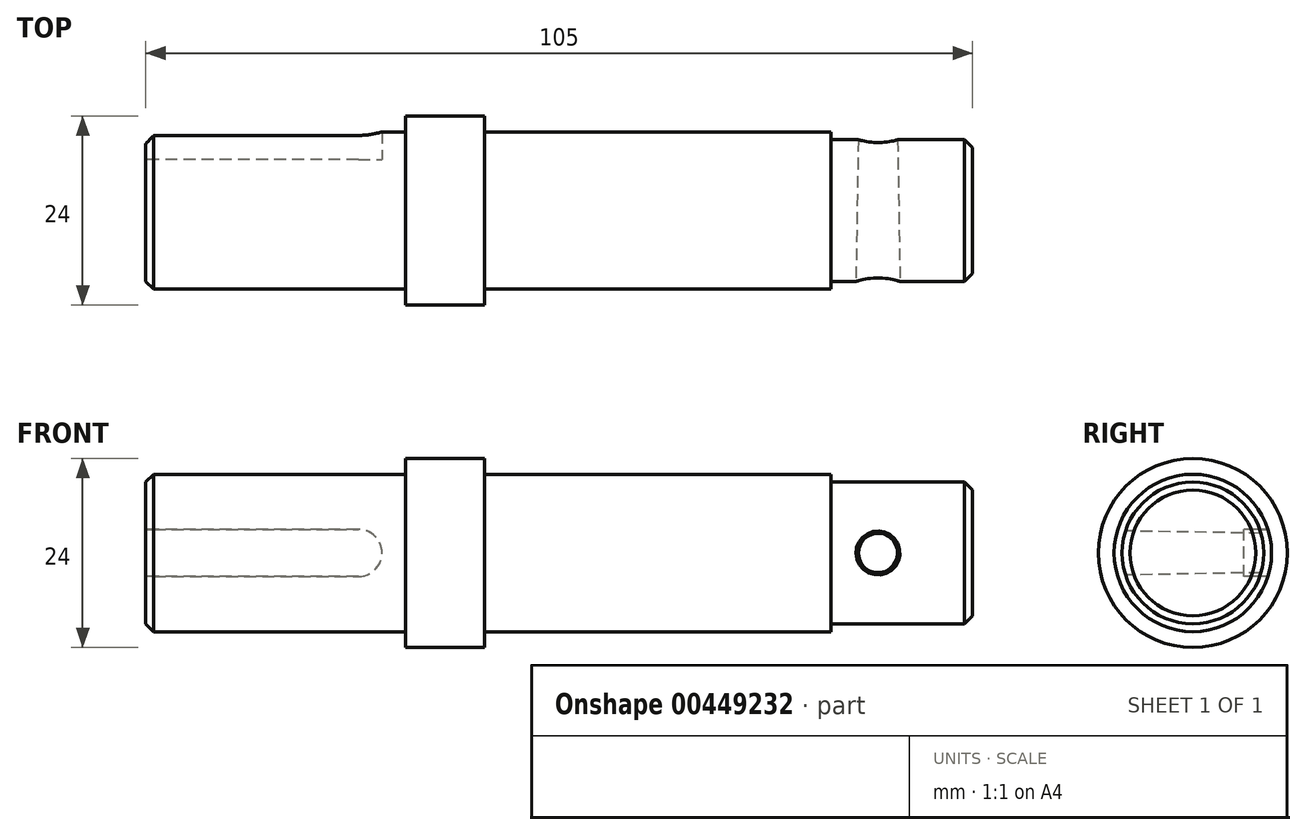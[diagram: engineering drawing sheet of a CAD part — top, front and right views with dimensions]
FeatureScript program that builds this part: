
annotation { "Feature Type Name" : "Feature", "Feature Type Description" : "" }
export const myFeature = defineFeature(function(context is Context, id is Id, definition is map)
    precondition{}
    {
        {
            var Q0;
            Q0=qCreatedBy(makeId("Right.planeOp"),FACE);
            var sketch = newSketch(context, id + "F0", { "sketchPlane" : qUnion([Q0])});
            skCircle(sketch, "E0", {"center": v(0, 0) * mm, "radius": 12 * mm});
            skSolve(sketch);
        }
        {
            var Q0;
            Q0 = qSketchRegion(id + "F0", true);
            extrude(context, id + "F1", {"entities" : qUnion([Q0]), "depth" : (105 - 18 - 33 - 44) * mm});
        }
        {
            var Q0;
            Q0=makeQuery(id+"F1.opExtrude","CAP_FACE",FACE,{"disambiguationData":[OSD([sQuery(id+"F0.wireOp",EDGE,"E0")])],"isStart":true});
            var sketch = newSketch(context, id + "F2", { "sketchPlane" : qUnion([Q0])});
            skCircle(sketch, "E1", {"center": v(0, 0) * mm, "radius": 10 * mm});
            skSolve(sketch);
        }
        {
            var Q0;
            Q0 = qSketchRegion(id + "F2", true);
            extrude(context, id + "F3", {"entities" : qUnion([Q0]), "operationType" : NewBodyOperationType.ADD, "depth" : 33 * mm});
        }
        {
            var Q0;
            Q0 = qSketchRegion(id + "F2", true);
            extrude(context, id + "F4", {"entities" : qUnion([Q0]), "operationType" : NewBodyOperationType.ADD, "oppositeDirection" : true, "depth" : (105 - 18 - 33) * mm});
        }
        {
            var Q0;
            Q0=makeQuery(id+"F4.opExtrude","CAP_FACE",FACE,{"disambiguationData":[OSD([sQuery(id+"F2.wireOp",EDGE,"E1")])],"isStart":false});
            var sketch = newSketch(context, id + "F5", { "sketchPlane" : qUnion([Q0])});
            skCircle(sketch, "E2", {"center": v(0, 0) * mm, "radius": 9 * mm});
            skSolve(sketch);
        }
        {
            var Q0;
            Q0 = qSketchRegion(id + "F5", true);
            extrude(context, id + "F6", {"entities" : qUnion([Q0]), "operationType" : NewBodyOperationType.ADD, "depth" : 18 * mm});
        }
        {
            var Q0;
            Q0=qCreatedBy(makeId("Front.planeOp"),FACE);
            cPlane(context, id + "F7", {"entities" : qUnion([Q0]), "cplaneType" : CPlaneType.OFFSET, "offset" : 6.5 * mm, "oppositeDirection" : true, "width" : 150 * mm, "height" : 150 * mm});
        }
        {
            var Q0;
            Q0=qCreatedBy(id+"F7.planeOp",FACE);
            var sketch = newSketch(context, id + "F8", { "sketchPlane" : qUnion([Q0])});
            skLineSegment(sketch, "E3.0", {"start": v(-33, -3) * mm, "end": v(-33, 3) * mm});
            skLineSegment(sketch, "E4.bottom", {"start": v(-6, -3) * mm, "end": v(-33, -3) * mm});
            skLineSegment(sketch, "E4.top", {"start": v(-6, 3) * mm, "end": v(-33, 3) * mm});
            skPoint(sketch, "E4.middle", {"position": v(-33, 0) * mm});
            skArc(sketch, "E5", {"start": v(-6, -3) * mm, "mid": v(-3, 0) * mm, "end": v(-6, 3) * mm});
            skPoint(sketch, "E5.centerSnap0", {"position": v(-3, 0) * mm});
            skPoint(sketch, "E6.orphan", {"position": v(-3, 3) * mm});
            skPoint(sketch, "E7.orphan", {"position": v(-3, -3) * mm});
            skPoint(sketch, "E4.right.end.orphan", {"position": v(-63, 3) * mm});
            skPoint(sketch, "E4.right.start.orphan", {"position": v(-63, -3) * mm});
            skPoint(sketch, "E8.orphan", {"position": v(-33, 10) * mm});
            skPoint(sketch, "E9.orphan", {"position": v(-33, -10) * mm});
            skSolve(sketch);
        }
        {
            var Q0;
            Q0 = qSketchRegion(id + "F8", true);
            extrude(context, id + "F9", {"entities" : qUnion([Q0]), "operationType" : NewBodyOperationType.REMOVE, "endBound" : BoundingType.THROUGH_ALL, "oppositeDirection" : true, "depth" : 25 * mm});
        }
        {
            var Q0;
            Q0=makeQuery(id+"F3.opExtrude","CAP_EDGE",EDGE,{"disambiguationData":[OSD([sQuery(id+"F2.wireOp",EDGE,"E1")])],"isStart":false});
            var Q1;
            Q1=makeQuery(id+"F6.opExtrude","CAP_EDGE",EDGE,{"disambiguationData":[OSD([sQuery(id+"F5.wireOp",EDGE,"E2")])],"isStart":false});
            chamfer(context, id + "F10", {"entities" : qUnion([Q0, Q1]), "width" : 1 * mm, "tangentPropagation" : true});
        }
        {
            var Q0;
            Q0=qCreatedBy(makeId("Top.planeOp"),FACE);
            var sketch = newSketch(context, id + "F11", { "sketchPlane" : qUnion([Q0])});
            skLineSegment(sketch, "E10", {"start": v(60, 13.35) * mm, "end": v(60, -14.26) * mm, "construction": true});
            skLineSegment(sketch, "E11", {"start": v(60, 9) * mm, "end": v(71, 9) * mm});
            skLineSegment(sketch, "E12", {"start": v(62.5, 9) * mm, "end": v(62.8, -9) * mm});
            skLineSegment(sketch, "E13", {"start": v(62.8, -9) * mm, "end": v(60, -9) * mm});
            skLineSegment(sketch, "E14", {"start": v(60, 9) * mm, "end": v(60, -9) * mm});
            skLineSegment(sketch, "E15", {"start": v(62.5, 9) * mm, "end": v(62.5, 9.98) * mm});
            skLineSegment(sketch, "E16", {"start": v(62.5, 9.98) * mm, "end": v(60, 9.98) * mm});
            skLineSegment(sketch, "E17", {"start": v(60, 9.98) * mm, "end": v(60, 9) * mm});
            skLineSegment(sketch, "E18", {"start": v(62.8, -9) * mm, "end": v(62.82, -10.02) * mm});
            skLineSegment(sketch, "E19", {"start": v(62.82, -10.02) * mm, "end": v(60, -10.02) * mm});
            skLineSegment(sketch, "E20", {"start": v(60, -10.02) * mm, "end": v(60, -9) * mm});
            skSolve(sketch);
        }
        {
            var Q0;
            Q0 = qSketchRegion(id + "F11", true);
            var Q1;
            Q1=sQuery(id+"F11.wireOp",EDGE,"E10");
            revolve(context, id + "F12", {"operationType" : NewBodyOperationType.REMOVE, "entities" : qUnion([Q0]), "axis" : qUnion([Q1]), "revolveType" : RevolveType.FULL, "oppositeDirection" : true});
        }
    });
